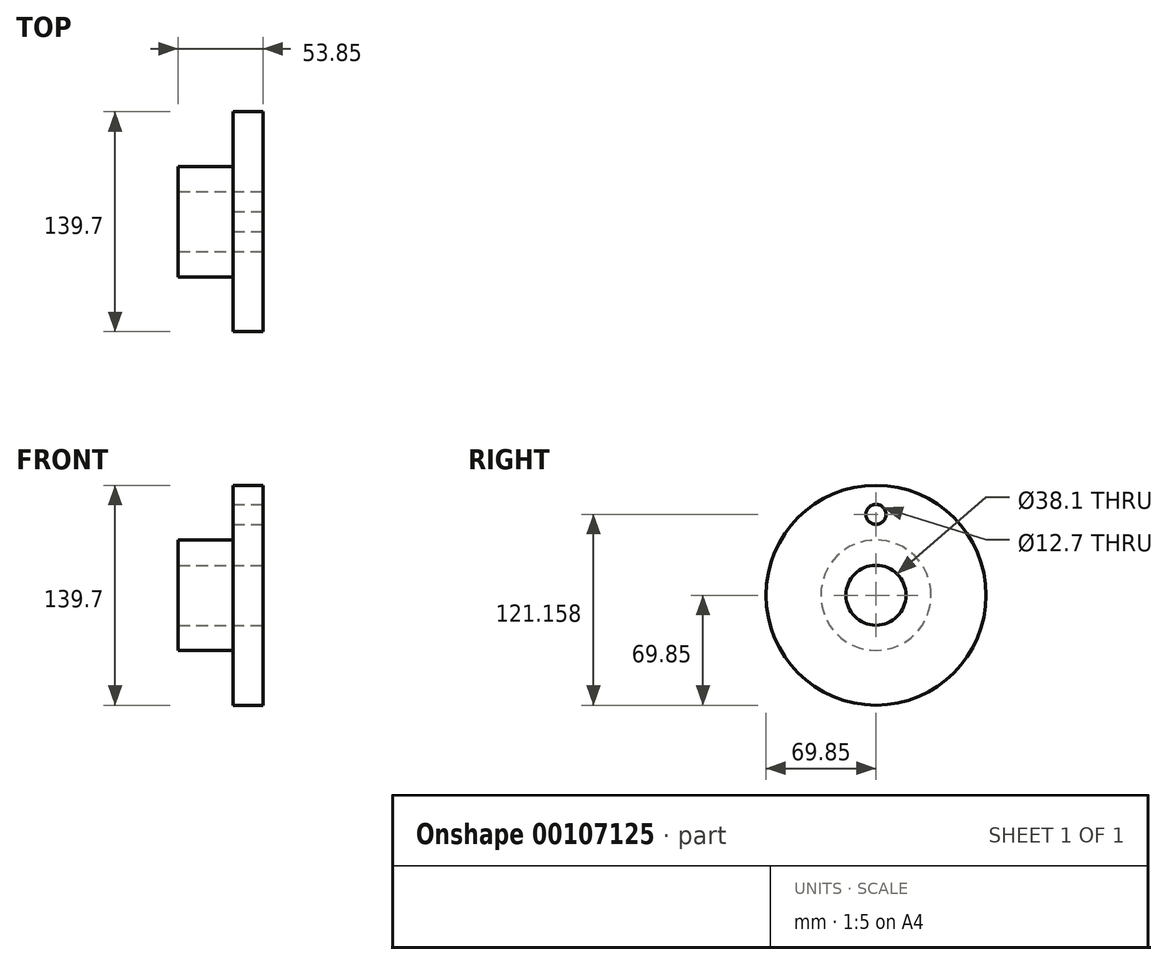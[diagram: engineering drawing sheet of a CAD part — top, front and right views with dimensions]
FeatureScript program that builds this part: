
annotation { "Feature Type Name" : "Feature", "Feature Type Description" : "" }
export const myFeature = defineFeature(function(context is Context, id is Id, definition is map)
    precondition{}
    {
        {
            var Q0;
            Q0=qCreatedBy(makeId("Front.planeOp"),FACE);
            var sketch = newSketch(context, id + "F0", { "sketchPlane" : qUnion([Q0])});
            skLineSegment(sketch, "E0", {"start": v(0, 0) * mm, "end": v(-61.45, 0) * mm, "construction": true});
            skLineSegment(sketch, "E1", {"start": v(0, 19.05) * mm, "end": v(0, 69.85) * mm});
            skLineSegment(sketch, "E2", {"start": v(0, 69.85) * mm, "end": v(-19.05, 69.85) * mm});
            skLineSegment(sketch, "E3", {"start": v(-19.05, 69.85) * mm, "end": v(-19.05, 35.05) * mm});
            skLineSegment(sketch, "E4", {"start": v(-19.05, 35.05) * mm, "end": v(-53.85, 35.05) * mm});
            skLineSegment(sketch, "E5", {"start": v(-53.85, 35.05) * mm, "end": v(-53.85, 19.05) * mm});
            skLineSegment(sketch, "E6", {"start": v(-53.85, 19.05) * mm, "end": v(0, 19.05) * mm});
            skSolve(sketch);
        }
        {
            var Q0;
            Q0=makeQuery(id+"F0.imprint","IMPRINT",FACE,{"disambiguationData":[TD([[makeQuery(id+"F0.imprint","IMPRINT",EDGE,{"derivedFrom":sQuery(id+"F0.wireOp",EDGE,"E1")}),1.0]])]});
            var Q1;
            Q1=sQuery(id+"F0.wireOp",EDGE,"E0");
            revolve(context, id + "F1", {"entities" : qUnion([Q0]), "axis" : qUnion([Q1]), "revolveType" : RevolveType.FULL});
        }
        {
            var Q0;
            Q0=qCreatedBy(makeId("Right.planeOp"),FACE);
            var sketch = newSketch(context, id + "F2", { "sketchPlane" : qUnion([Q0])});
            skCircle(sketch, "E7", {"center": v(0, 51.3) * mm, "radius": 6.35 * mm});
            skSolve(sketch);
        }
        {
            var Q0;
            Q0 = qSketchRegion(id + "F2", true);
            extrude(context, id + "F3", {"entities" : qUnion([Q0]), "operationType" : NewBodyOperationType.REMOVE, "oppositeDirection" : true, "depth" : 25.4 * mm});
        }
    });
